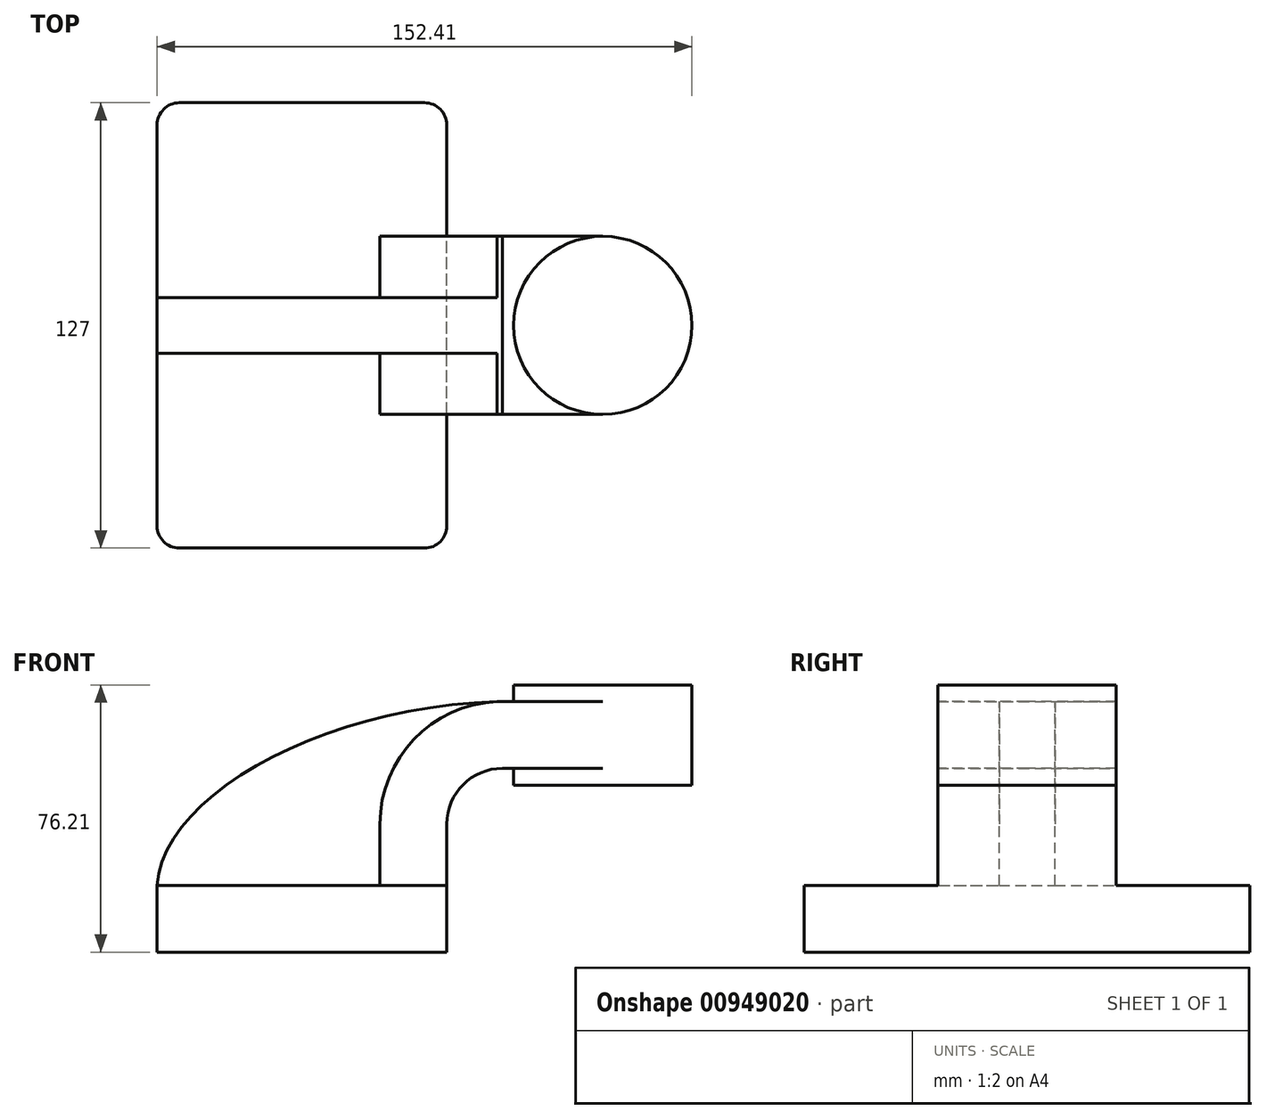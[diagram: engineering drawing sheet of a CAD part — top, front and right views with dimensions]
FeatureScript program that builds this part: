
annotation { "Feature Type Name" : "Feature", "Feature Type Description" : "" }
export const myFeature = defineFeature(function(context is Context, id is Id, definition is map)
    precondition{}
    {
        {
            var Q0;
            Q0=qCreatedBy(makeId("Front.planeOp"),FACE);
            var sketch = newSketch(context, id + "F0", { "sketchPlane" : qUnion([Q0])});
            skLineSegment(sketch, "E0.bottom", {"start": v(41.28, -9.52) * mm, "end": v(-41.28, -9.53) * mm});
            skLineSegment(sketch, "E0.top", {"start": v(41.28, 9.53) * mm, "end": v(-41.28, 9.53) * mm});
            skLineSegment(sketch, "E0.left", {"start": v(41.28, -9.52) * mm, "end": v(41.28, 9.53) * mm});
            skLineSegment(sketch, "E0.right", {"start": v(-41.28, -9.53) * mm, "end": v(-41.28, 9.53) * mm});
            skPoint(sketch, "E0.middle", {"position": v(0, 0) * mm});
            skLineSegment(sketch, "E1", {"start": v(41.28, 9.53) * mm, "end": v(41.28, 27) * mm});
            skArc(sketch, "E2", {"start": v(41.28, 27) * mm, "mid": v(45.92, 38.23) * mm, "end": v(57.15, 42.88) * mm});
            skLineSegment(sketch, "E3", {"start": v(57.15, 42.88) * mm, "end": v(85.72, 42.88) * mm});
            skLineSegment(sketch, "E4.bottom", {"start": v(111.12, 38.1) * mm, "end": v(60.32, 38.1) * mm});
            skLineSegment(sketch, "E4.top", {"start": v(111.12, 66.68) * mm, "end": v(60.32, 66.68) * mm});
            skLineSegment(sketch, "E4.left", {"start": v(111.12, 38.1) * mm, "end": v(111.12, 66.68) * mm});
            skLineSegment(sketch, "E4.right", {"start": v(60.32, 38.1) * mm, "end": v(60.32, 66.68) * mm});
            skPoint(sketch, "E4.middle", {"position": v(85.72, 52.39) * mm});
            skLineSegment(sketch, "E5.0", {"start": v(57.15, 61.93) * mm, "end": v(85.72, 61.93) * mm});
            skArc(sketch, "E5.1", {"start": v(22.23, 27) * mm, "mid": v(32.45, 51.7) * mm, "end": v(57.15, 61.93) * mm});
            skLineSegment(sketch, "E5.2", {"start": v(22.22, 9.53) * mm, "end": v(22.22, 27) * mm});
            skLineSegment(sketch, "E6", {"start": v(85.72, 38.1) * mm, "end": v(85.72, 66.68) * mm});
            skFitSpline(sketch, "E7", {"points": [v(-41.28, 9.53) * mm, v(57.15, 61.93) * mm], "startDerivative": vector(5.07, 78.42) * mm, "endDerivative": vector(149.65, 2.6) * mm});
            skSolve(sketch);
        }
        {
            var Q0;
            Q0=makeQuery(id+"F0.imprint","IMPRINT",FACE,{"disambiguationData":[TD([[makeQuery(id+"F0.imprint","IMPRINT",EDGE,{"derivedFrom":sQuery(id+"F0.wireOp",EDGE,"E0.bottom")}),-1.0]])]});
            extrude(context, id + "F1", {"entities" : qUnion([Q0]), "endBound" : BoundingType.SYMMETRIC, "depth" : 127 * mm, "offsetDistance" : 25.4 * mm});
        }
        {
            var Q0;
            {var subQ4=sQuery(id+"F0.wireOp",EDGE,"E1");Q0=makeQuery(id+"F0.imprint","IMPRINT",FACE,{"disambiguationData":[TD([[makeQuery(id+"F0.imprint","IMPRINT",EDGE,{"derivedFrom":subQ4}),1.0]])]});}
            var Q1;
            {var subQ0=sQuery(id+"F0.wireOp",EDGE,"E6");var subQ1=sQuery(id+"F0.wireOp",EDGE,"E3");var subQ2=makeQuery(id+"F0.imprint","INTERSECT",VERTEX,{"derivedFrom":[subQ1,subQ0]});Q1=makeQuery(id+"F0.imprint","IMPRINT",FACE,{"disambiguationData":[TD([[makeQuery(id+"F0.imprint","IMPRINT",EDGE,{"disambiguationData":[TD([[subQ2,1.0]])],"derivedFrom":subQ1}),1.0]])]});}
            extrude(context, id + "F2", {"entities" : qUnion([Q0, Q1]), "operationType" : NewBodyOperationType.ADD, "endBound" : BoundingType.SYMMETRIC, "depth" : 50.8 * mm, "offsetDistance" : 25.4 * mm});
        }
        {
            var Q0;
            {var subQ3=sQuery(id+"F0.wireOp",EDGE,"E5.2");Q0=makeQuery(id+"F0.imprint","IMPRINT",FACE,{"disambiguationData":[TD([[makeQuery(id+"F0.imprint","IMPRINT",EDGE,{"derivedFrom":subQ3}),1.0]])]});}
            extrude(context, id + "F3", {"entities" : qUnion([Q0]), "operationType" : NewBodyOperationType.ADD, "endBound" : BoundingType.SYMMETRIC, "depth" : 15.88 * mm, "offsetDistance" : 25.4 * mm});
        }
        {
            var Q0;
            {var subQ4=sQuery(id+"F0.wireOp",EDGE,"E4.left");Q0=makeQuery(id+"F0.imprint","IMPRINT",FACE,{"disambiguationData":[TD([[makeQuery(id+"F0.imprint","IMPRINT",EDGE,{"derivedFrom":subQ4}),1.0]])]});}
            var Q1;
            Q1=sQuery(id+"F0.wireOp",EDGE,"E6");
            revolve(context, id + "F4", {"operationType" : NewBodyOperationType.ADD, "surfaceOperationType" : NewSurfaceOperationType.NEW, "entities" : qUnion([Q0]), "axis" : qUnion([Q1]), "revolveType" : RevolveType.FULL});
        }
        {
            var Q0;
            Q0=makeQuery(id+"F1.opExtrude","CAP_EDGE",EDGE,{"disambiguationData":[OSD([sQuery(id+"F0.wireOp",EDGE,"E0.right")])],"isStart":false});
            var Q1;
            Q1=makeQuery(id+"F1.opExtrude","CAP_EDGE",EDGE,{"disambiguationData":[OSD([sQuery(id+"F0.wireOp",EDGE,"E0.left")])],"isStart":false});
            var Q2;
            Q2=makeQuery(id+"F1.opExtrude","CAP_EDGE",EDGE,{"disambiguationData":[OSD([sQuery(id+"F0.wireOp",EDGE,"E0.left")])],"isStart":true});
            var Q3;
            Q3=makeQuery(id+"F1.opExtrude","CAP_EDGE",EDGE,{"disambiguationData":[OSD([sQuery(id+"F0.wireOp",EDGE,"E0.right")])],"isStart":true});
            fillet(context, id + "F5", {"entities" : qUnion([Q0, Q1, Q2, Q3]), "radius" : 6.35 * mm, "tangentPropagation" : true, "allowEdgeOverflow" : false});
        }
    });
